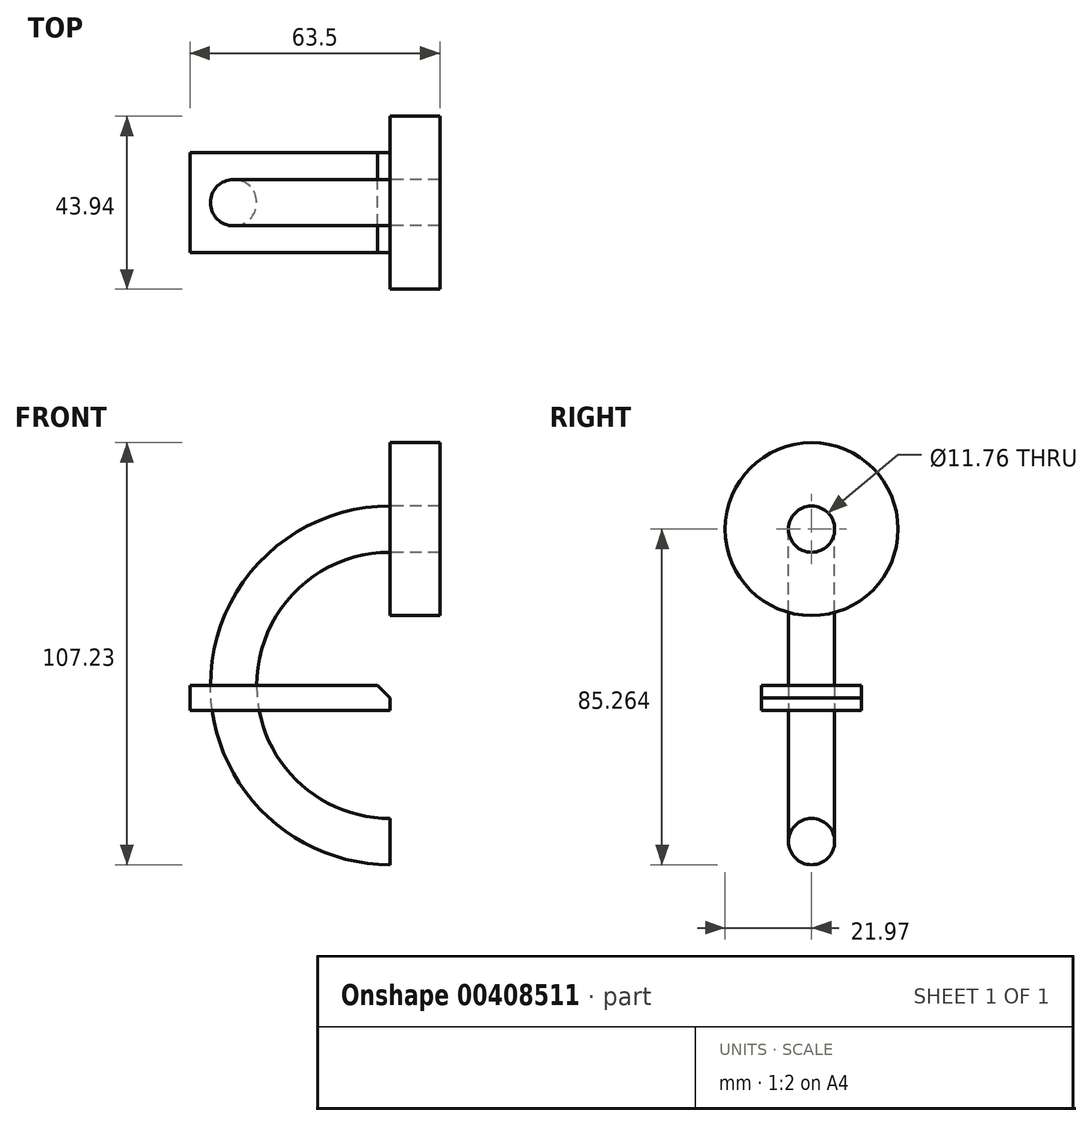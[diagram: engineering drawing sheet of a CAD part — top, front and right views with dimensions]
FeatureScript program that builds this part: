
annotation { "Feature Type Name" : "Feature", "Feature Type Description" : "" }
export const myFeature = defineFeature(function(context is Context, id is Id, definition is map)
    precondition{}
    {
        {
            var Q0;
            Q0=qCreatedBy(makeId("Top.planeOp"),FACE);
            var sketch = newSketch(context, id + "F0", { "sketchPlane" : qUnion([Q0])});
            skLineSegment(sketch, "E0.bottom", {"start": v(25.4, -12.7) * mm, "end": v(-25.4, -12.7) * mm});
            skLineSegment(sketch, "E0.top", {"start": v(25.4, 12.7) * mm, "end": v(-25.4, 12.7) * mm});
            skLineSegment(sketch, "E0.left", {"start": v(25.4, -12.7) * mm, "end": v(25.4, 12.7) * mm});
            skLineSegment(sketch, "E0.right", {"start": v(-25.4, -12.7) * mm, "end": v(-25.4, 12.7) * mm});
            skPoint(sketch, "E0.middle", {"position": v(0, 0) * mm});
            skSolve(sketch);
        }
        {
            var Q0;
            Q0 = qSketchRegion(id + "F0", true);
            extrude(context, id + "F1", {"entities" : qUnion([Q0]), "depth" : 6.35 * mm});
        }
        {
            var Q0;
            Q0=makeQuery(id+"F1.opExtrude","CAP_FACE",FACE,{"disambiguationData":[OSD([sQuery(id+"F0.wireOp",EDGE,"E0.bottom"),sQuery(id+"F0.wireOp",EDGE,"E0.top"),sQuery(id+"F0.wireOp",EDGE,"E0.left"),sQuery(id+"F0.wireOp",EDGE,"E0.right")])],"isStart":false});
            var sketch = newSketch(context, id + "F2", { "sketchPlane" : qUnion([Q0])});
            skCircle(sketch, "E1", {"center": v(-14.3, 0) * mm, "radius": 5.88 * mm});
            skSolve(sketch);
        }
        {
            var Q0;
            Q0=makeQuery(id+"F2.imprint","IMPRINT",FACE,{"disambiguationData":[TD([[makeQuery(id+"F2.imprint","IMPRINT",EDGE,{"derivedFrom":sQuery(id+"F2.wireOp",EDGE,"E1")}),1.0]])]});
            var Q1;
            Q1=sQuery(id+"F2.wireOp",EDGE,"E1");
            var Q2;
            Q2=makeQuery(id+"F1.opExtrude","CAP_EDGE",EDGE,{"disambiguationData":[OSD([sQuery(id+"F0.wireOp",EDGE,"E0.left")])],"isStart":false});
            revolve(context, id + "F3", {"entities" : qUnion([Q0]), "surfaceEntities" : qUnion([Q1]), "axis" : qUnion([Q2]), "revolveType" : RevolveType.ONE_DIRECTION, "angle" : 90 * degree});
        }
        {
            var Q0;
            Q0=makeQuery(id+"F3.opRevolve","CAP_FACE",FACE,{"disambiguationData":[OSD([sQuery(id+"F2.wireOp",EDGE,"E1")])],"isStart":false});
            var sketch = newSketch(context, id + "F4", { "sketchPlane" : qUnion([Q0])});
            skCircle(sketch, "E2", {"center": v(0, 46.04) * mm, "radius": 21.97 * mm});
            skSolve(sketch);
        }
        {
            var Q0;
            Q0=makeQuery(id+"F4.imprint","IMPRINT",FACE,{"disambiguationData":[TD([[makeQuery(id+"F4.imprint","IMPRINT",EDGE,{"derivedFrom":sQuery(id+"F4.wireOp",EDGE,"E2")}),1.0]])]});
            var Q1;
            Q1=sQuery(id+"F4.wireOp",EDGE,"E2");
            extrude(context, id + "F5", {"entities" : qUnion([Q0]), "surfaceEntities" : qUnion([Q1]), "depth" : 12.7 * mm});
        }
        {
            var Q0;
            Q0=makeQuery(id+"F3.opRevolve","SWEPT_BODY",BODY,{"disambiguationData":[OSD([sQuery(id+"F2.wireOp",EDGE,"E1")])]});
            var Q1;
            Q1=makeQuery(id+"F1.opExtrude","CAP_FACE",FACE,{"disambiguationData":[OSD([sQuery(id+"F0.wireOp",EDGE,"E0.bottom"),sQuery(id+"F0.wireOp",EDGE,"E0.top"),sQuery(id+"F0.wireOp",EDGE,"E0.left"),sQuery(id+"F0.wireOp",EDGE,"E0.right")])],"isStart":false});
            mirror(context, id + "F6", {"entities" : qUnion([Q0]), "mirrorPlane" : qUnion([Q1])});
        }
        {
            var Q0;
            Q0=makeQuery(id+"F1.opExtrude","CAP_EDGE",EDGE,{"disambiguationData":[OSD([sQuery(id+"F0.wireOp",EDGE,"E0.left")])],"isStart":false});
            chamfer(context, id + "F7", {"entities" : qUnion([Q0]), "width" : 3.17 * mm, "tangentPropagation" : true});
        }
    });
